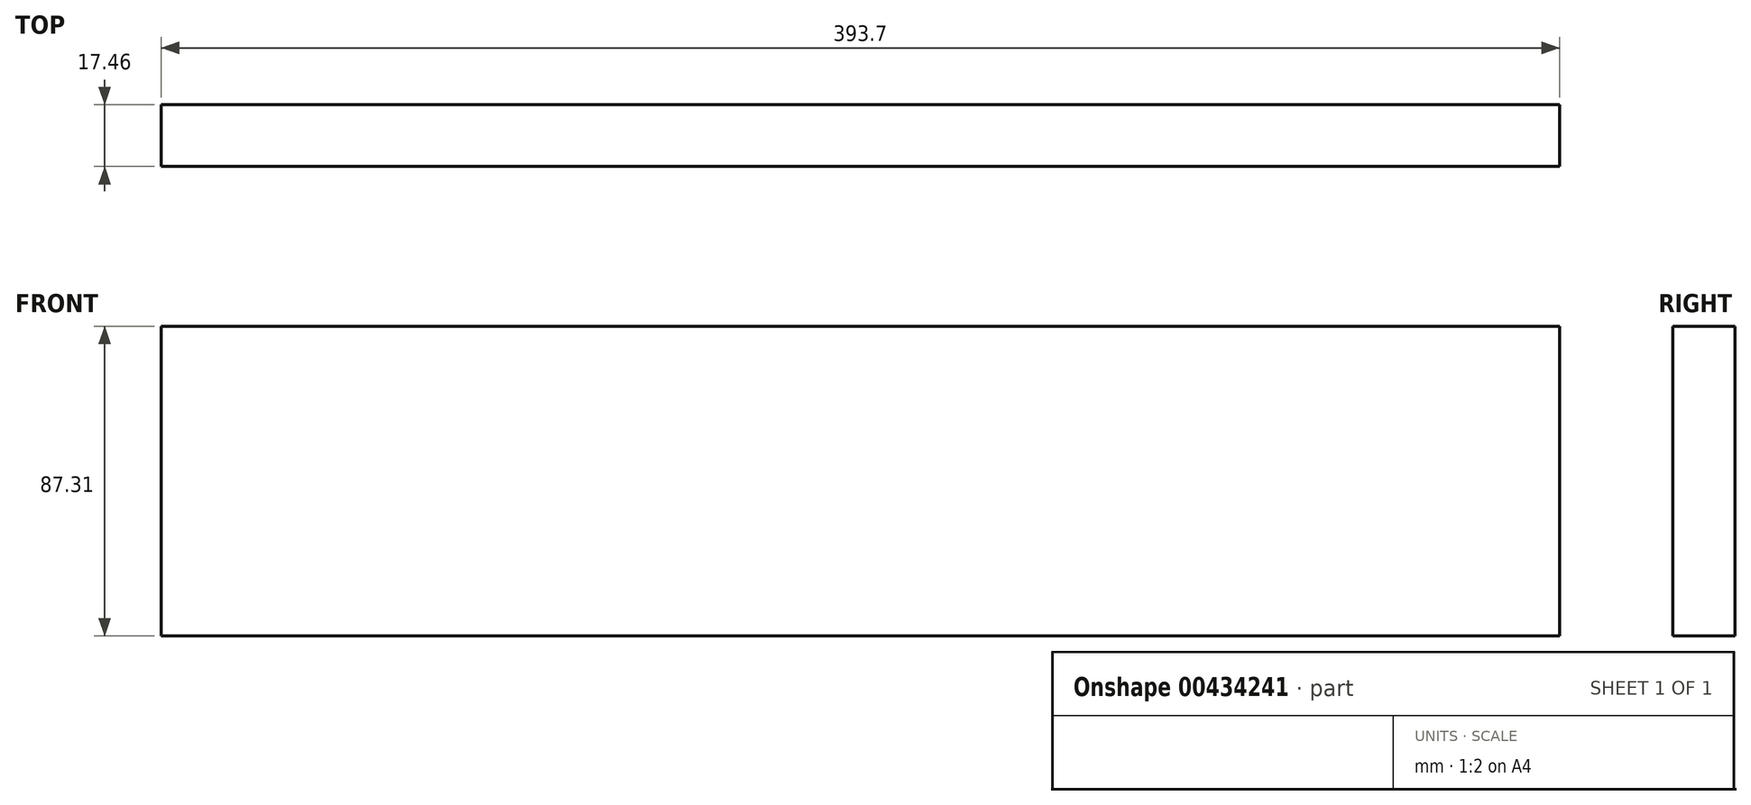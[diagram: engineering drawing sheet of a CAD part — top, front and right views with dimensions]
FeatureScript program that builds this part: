
annotation { "Feature Type Name" : "Feature", "Feature Type Description" : "" }
export const myFeature = defineFeature(function(context is Context, id is Id, definition is map)
    precondition{}
    {
        {
            var Q0;
            Q0=qCreatedBy(makeId("Front.planeOp"),FACE);
            var sketch = newSketch(context, id + "F0", { "sketchPlane" : qUnion([Q0])});
            skLineSegment(sketch, "E0.bottom", {"start": v(0, 0) * mm, "end": v(393.7, 0) * mm});
            skLineSegment(sketch, "E0.top", {"start": v(0, 87.31) * mm, "end": v(393.7, 87.31) * mm});
            skLineSegment(sketch, "E0.left", {"start": v(0, 0) * mm, "end": v(0, 87.31) * mm});
            skLineSegment(sketch, "E0.right", {"start": v(393.7, 0) * mm, "end": v(393.7, 87.31) * mm});
            skSolve(sketch);
        }
        {
            var Q0;
            Q0 = qSketchRegion(id + "F0", true);
            extrude(context, id + "F1", {"entities" : qUnion([Q0]), "depth" : 17.46 * mm});
        }
    });
